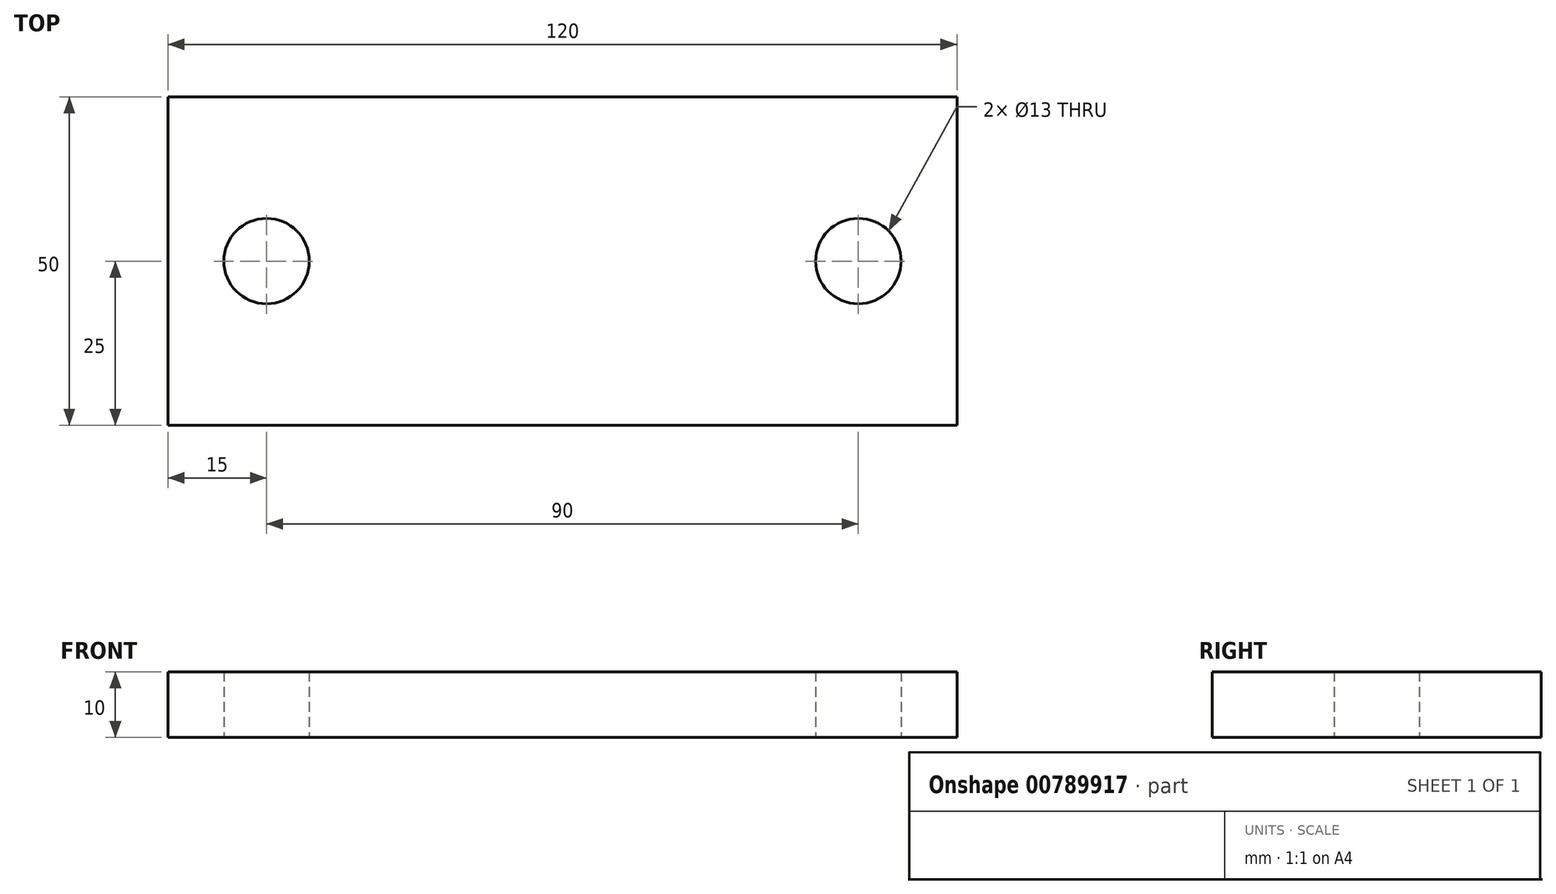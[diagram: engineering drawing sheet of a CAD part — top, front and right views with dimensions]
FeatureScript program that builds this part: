
annotation { "Feature Type Name" : "Feature", "Feature Type Description" : "" }
export const myFeature = defineFeature(function(context is Context, id is Id, definition is map)
    precondition{}
    {
        {
            var Q0;
            Q0=qCreatedBy(makeId("Top.planeOp"),FACE);
            var sketch = newSketch(context, id + "F0", { "sketchPlane" : qUnion([Q0])});
            skLineSegment(sketch, "E0.bottom", {"start": v(60, 25) * mm, "end": v(-60, 25) * mm});
            skLineSegment(sketch, "E0.top", {"start": v(60, -25) * mm, "end": v(-60, -25) * mm});
            skLineSegment(sketch, "E0.left", {"start": v(60, 25) * mm, "end": v(60, -25) * mm});
            skLineSegment(sketch, "E0.right", {"start": v(-60, 25) * mm, "end": v(-60, -25) * mm});
            skPoint(sketch, "E0.middle", {"position": v(0, 0) * mm});
            skCircle(sketch, "E1", {"center": v(-45, 0) * mm, "radius": 6.5 * mm});
            skCircle(sketch, "E2.MirrorC", {"center": v(45, 0) * mm, "radius": 6.5 * mm});
            skSolve(sketch);
        }
        {
            var Q0;
            Q0=qSketchRegion(id+"F0",true);
            extrude(context, id + "F1", {"entities" : qUnion([Q0]), "depth" : 10 * mm, "offsetDistance" : 25 * mm});
        }
    });
